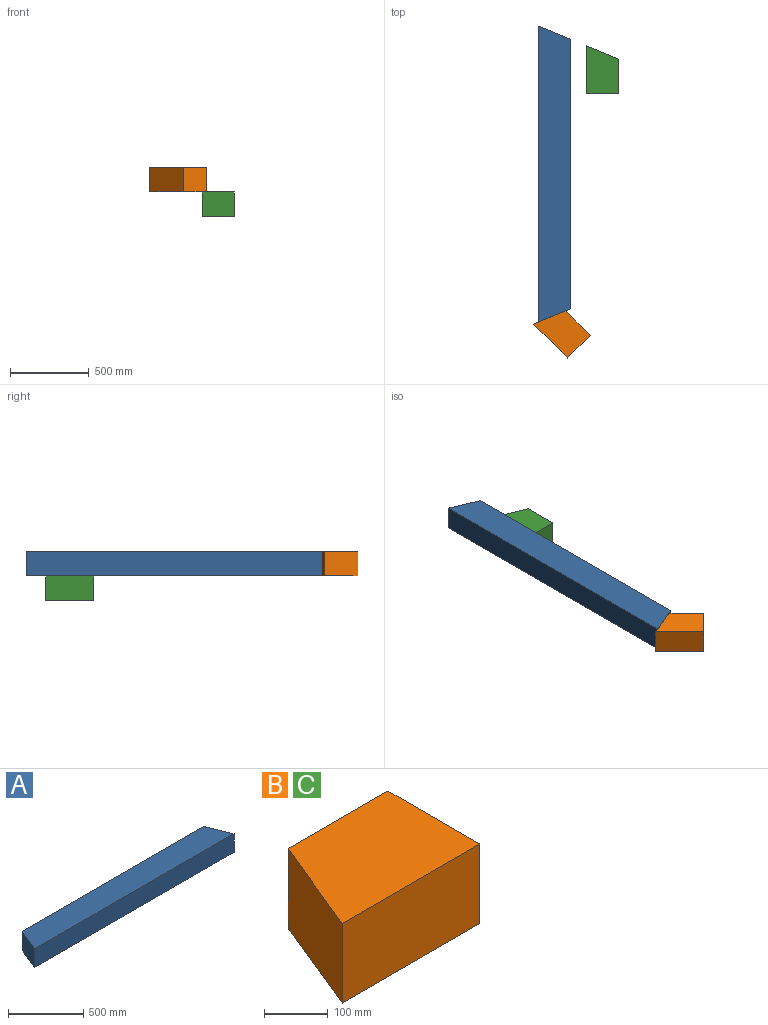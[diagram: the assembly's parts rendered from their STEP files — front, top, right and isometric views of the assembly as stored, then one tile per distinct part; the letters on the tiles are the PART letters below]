
ASSEMBLY  parts=3 mates=4
PART A: 6 faces, bbox 1879.6x203.2x152.4 mm
  f0: plane 1879.6x203.2mm, normal (0,0,1), area 364831.7mm2, adj f2,f3,f4,f5
  f1: plane 1879.6x203.2mm, normal (0,0,-1), area 364831.7mm2, adj f2,f3,f4,f5
  f2: plane 1711.26x152.4mm, normal (0,1,0), area 260796.6mm2, adj f0,f1,f4,f5
  f3: plane 1879.6x152.4mm, normal (0,-1,0), area 286451mm2, adj f0,f1,f4,f5
  f4: plane 203.2x152.4mm, normal (-0.92,0.38,0), area 33519.2mm2, adj f0,f1,f2,f3
  f5: plane 203.2x152.4mm, normal (0.92,0.38,0), area 33519.2mm2, adj f0,f1,f2,f3
PART B: 6 faces, bbox 304.8x203.2x152.4 mm
  f0: plane 220.63x152.4mm, normal (0,1,0), area 33624.3mm2, adj f2,f3,f4,f5
  f1: plane 304.8x152.4mm, normal (0,-1,0), area 46451.5mm2, adj f2,f3,f4,f5
  f2: plane 304.8x203.2mm, normal (0,0,-1), area 53383.9mm2, adj f0,f1,f4,f5
  f3: plane 304.8x203.2mm, normal (0,0,1), area 53383.9mm2, adj f0,f1,f4,f5
  f4: plane 203.2x152.4mm, normal (1,0,0), area 30967.7mm2, adj f0,f1,f2,f3
  f5: plane 203.2x152.4mm, normal (-0.92,0.38,0), area 33519.2mm2, adj f0,f1,f2,f3
PART C: same geometry as B
PLACE A rot(axis=(0,0,-1),90deg) t=(919.76,1092.99,76.57)mm fixed
PLACE B rot(axis=(0,0,-1),45deg) t=(967.56,104.76,76.57)mm
PLACE C rot(axis=(0,0,-1),90deg) t=(1223.21,1754.7,-75.83)mm
MATE planar B.f5 <-> A.f5  axis (-0.38,0.92,0) through (889.55,182.76,76.57)mm
MATE planar C.f3 <-> A.f1  axis (0,0,1) through (1217.79,1734.78,0.37)mm
MATE planar B.f3 <-> A.f0  axis (0,0,1) through (977.81,86.84,152.77)mm
MATE planar C.f5 <-> A.f4  axis (0.38,0.92,0) through (1223.21,1865.01,-75.83)mm
